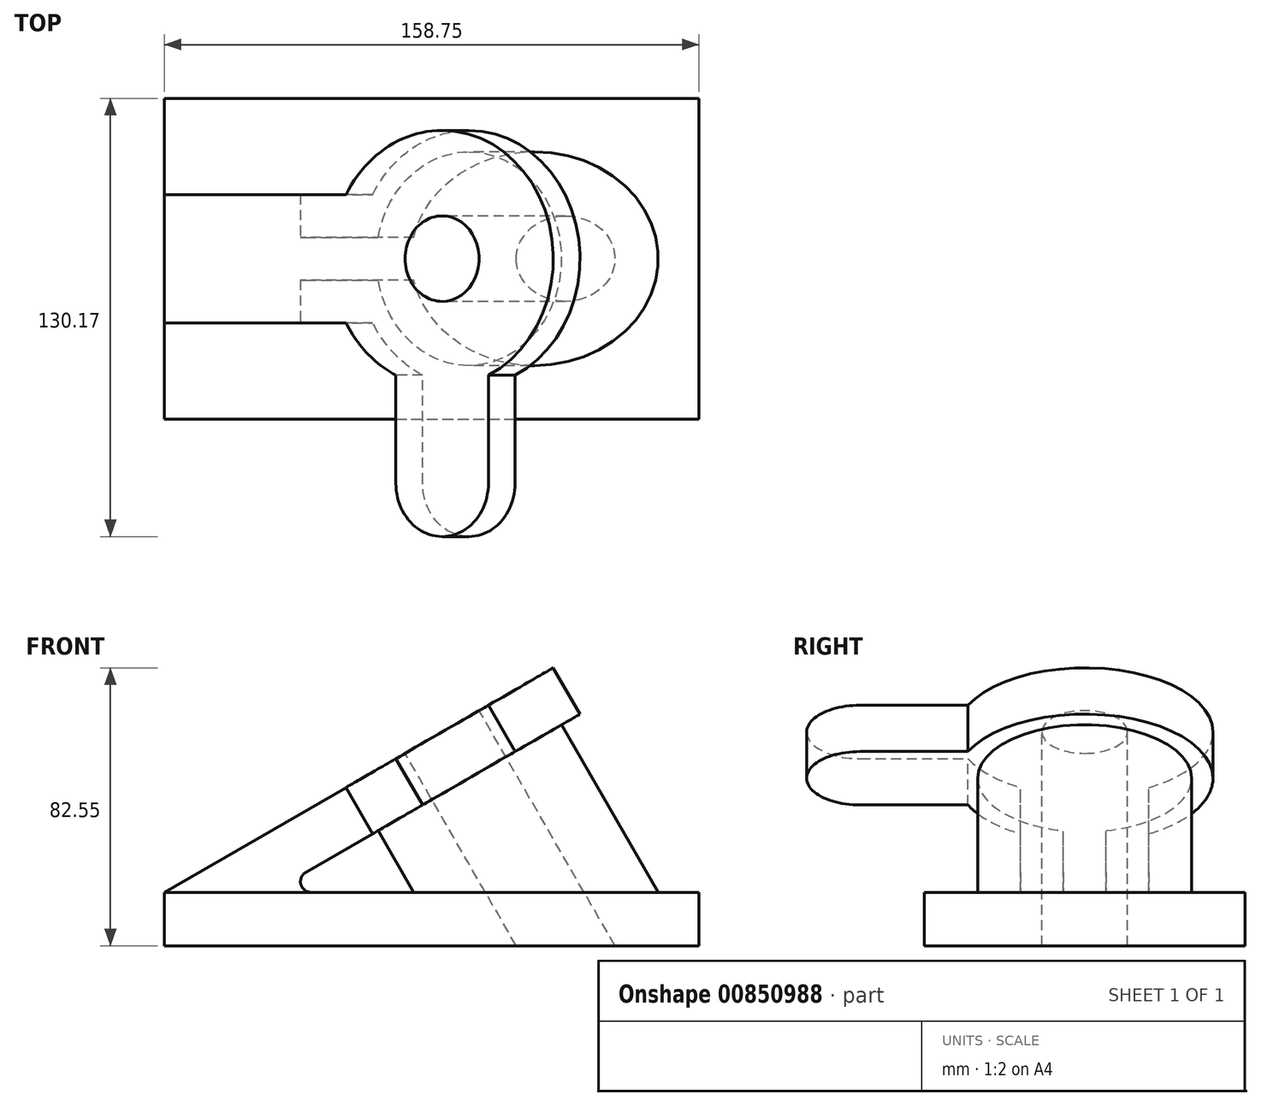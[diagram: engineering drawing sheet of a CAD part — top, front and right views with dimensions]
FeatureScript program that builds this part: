
annotation { "Feature Type Name" : "Feature", "Feature Type Description" : "" }
export const myFeature = defineFeature(function(context is Context, id is Id, definition is map)
    precondition{}
    {
        {
            var Q0;
            Q0=qCreatedBy(makeId("Front.planeOp"),FACE);
            var sketch = newSketch(context, id + "F0", { "sketchPlane" : qUnion([Q0])});
            skLineSegment(sketch, "E0.bottom", {"start": v(0, 0) * mm, "end": v(158.75, 0) * mm});
            skLineSegment(sketch, "E0.top", {"start": v(0, 15.88) * mm, "end": v(158.75, 15.88) * mm});
            skLineSegment(sketch, "E0.left", {"start": v(0, 0) * mm, "end": v(0, 15.87) * mm});
            skLineSegment(sketch, "E0.right", {"start": v(158.75, 0) * mm, "end": v(158.75, 15.88) * mm});
            skSolve(sketch);
        }
        {
            var Q0;
            Q0 = qSketchRegion(id + "F0", true);
            extrude(context, id + "F1", {"entities" : qUnion([Q0]), "oppositeDirection" : true, "depth" : 95.25 * mm, "offsetDistance" : 25.4 * mm});
        }
        {
            var Q0;
            Q0=makeQuery(id+"F1.opExtrude","SWEPT_EDGE",EDGE,{"disambiguationData":[OSD([sQuery(id+"F0.wireOp",EDGE,"E0.top"),sQuery(id+"F0.wireOp",EDGE,"E0.left")])]});
            var Q1;
            Q1=makeQuery(id+"F1.opExtrude","SWEPT_FACE",FACE,{"disambiguationData":[OSD([sQuery(id+"F0.wireOp",EDGE,"E0.top")])]});
            cPlane(context, id + "F2", {"entities" : qUnion([Q0, Q1]), "cplaneType" : CPlaneType.LINE_ANGLE, "offset" : 25.4 * mm, "angle" : 30 * degree, "width" : 152.4 * mm, "height" : 152.4 * mm});
        }
        {
            var Q0;
            Q0=qCreatedBy(id+"F2.planeOp",FACE);
            var sketch = newSketch(context, id + "F3", { "sketchPlane" : qUnion([Q0])});
            skArc(sketch, "E1", {"start": v(70.2, -66.67) * mm, "mid": v(131.36, -73.27) * mm, "end": v(119.06, -12.99) * mm});
            skLineSegment(sketch, "E2.bottom", {"start": v(7.94, -28.57) * mm, "end": v(70.2, -28.57) * mm});
            skLineSegment(sketch, "E2.top", {"start": v(7.94, -66.67) * mm, "end": v(70.2, -66.67) * mm});
            skLineSegment(sketch, "E2.left", {"start": v(7.94, -28.57) * mm, "end": v(7.94, -66.67) * mm});
            skPoint(sketch, "E2.middle", {"position": v(65.09, -47.63) * mm});
            skCircle(sketch, "E3", {"center": v(103.19, -47.63) * mm, "radius": 12.7 * mm});
            skArc(sketch, "E4", {"start": v(119.06, 19.05) * mm, "mid": v(103.19, 34.93) * mm, "end": v(87.31, 19.05) * mm});
            skLineSegment(sketch, "E5", {"start": v(119.06, 19.05) * mm, "end": v(119.06, -12.99) * mm});
            skLineSegment(sketch, "E6", {"start": v(87.31, 19.05) * mm, "end": v(87.31, -12.99) * mm});
            skArc(sketch, "E7.trimOffspring", {"start": v(87.31, -12.99) * mm, "mid": v(77.54, -19.45) * mm, "end": v(70.2, -28.58) * mm});
            skSolve(sketch);
        }
        {
            var Q0;
            Q0 = qSketchRegion(id + "F3", true);
            extrude(context, id + "F4", {"entities" : qUnion([Q0]), "operationType" : NewBodyOperationType.ADD, "depth" : 15.88 * mm, "offsetDistance" : 25.4 * mm});
        }
        {
            var Q0;
            Q0=makeQuery(id+"F4.opExtrude","CAP_FACE",FACE,{"disambiguationData":[OSD([sQuery(id+"F3.wireOp",EDGE,"E1"),sQuery(id+"F3.wireOp",EDGE,"E2.bottom"),sQuery(id+"F3.wireOp",EDGE,"E2.top"),sQuery(id+"F3.wireOp",EDGE,"E2.left"),sQuery(id+"F3.wireOp",EDGE,"E3"),sQuery(id+"F3.wireOp",EDGE,"E4"),sQuery(id+"F3.wireOp",EDGE,"E5"),sQuery(id+"F3.wireOp",EDGE,"E6"),sQuery(id+"F3.wireOp",EDGE,"E7.trimOffspring")])],"isStart":false});
            var sketch = newSketch(context, id + "F5", { "sketchPlane" : qUnion([Q0])});
            skCircle(sketch, "E8", {"center": v(103.19, -47.63) * mm, "radius": 12.7 * mm});
            skCircle(sketch, "E9", {"center": v(103.19, -47.63) * mm, "radius": 31.75 * mm});
            skSolve(sketch);
        }
        {
            var Q0;
            Q0=makeQuery(id+"F5.imprint","IMPRINT",FACE,{"disambiguationData":[TD([[makeQuery(id+"F5.imprint","IMPRINT",EDGE,{"derivedFrom":sQuery(id+"F5.wireOp",EDGE,"E8")}),-1.0]])]});
            var Q1;
            Q1=makeQuery(id+"F1.opExtrude","SWEPT_FACE",FACE,{"disambiguationData":[OSD([sQuery(id+"F0.wireOp",EDGE,"E0.top")])]});
            extrude(context, id + "F6", {"entities" : qUnion([Q0]), "operationType" : NewBodyOperationType.ADD, "endBound" : BoundingType.UP_TO_SURFACE, "depth" : 25.4 * mm, "endBoundEntityFace" : qUnion([Q1]), "offsetDistance" : 25.4 * mm});
        }
        {
            var Q0;
            Q0=makeQuery(id+"F4.opExtrude","CAP_FACE",FACE,{"disambiguationData":[OSD([sQuery(id+"F3.wireOp",EDGE,"E1"),sQuery(id+"F3.wireOp",EDGE,"E2.bottom"),sQuery(id+"F3.wireOp",EDGE,"E2.top"),sQuery(id+"F3.wireOp",EDGE,"E2.left"),sQuery(id+"F3.wireOp",EDGE,"E3"),sQuery(id+"F3.wireOp",EDGE,"E4"),sQuery(id+"F3.wireOp",EDGE,"E5"),sQuery(id+"F3.wireOp",EDGE,"E6"),sQuery(id+"F3.wireOp",EDGE,"E7.trimOffspring")])],"isStart":true});
            var sketch = newSketch(context, id + "F7", { "sketchPlane" : qUnion([Q0])});
            skCircle(sketch, "E10", {"center": v(103.19, 47.63) * mm, "radius": 12.7 * mm});
            skSolve(sketch);
        }
        {
            var Q0;
            Q0=makeQuery(id+"F7.imprint","IMPRINT",FACE,{"disambiguationData":[TD([[makeQuery(id+"F7.imprint","IMPRINT",EDGE,{"derivedFrom":sQuery(id+"F7.wireOp",EDGE,"E10")}),-1.0]])]});
            extrude(context, id + "F8", {"entities" : qUnion([Q0]), "operationType" : NewBodyOperationType.REMOVE, "endBound" : BoundingType.THROUGH_ALL, "oppositeDirection" : true, "depth" : 25.4 * mm, "offsetDistance" : 25.4 * mm});
        }
        {
            var Q0;
            {var subQ1=sQuery(id+"F0.wireOp",EDGE,"E0.left");var subQ2=sQuery(id+"F0.wireOp",EDGE,"E0.top");Q0=makeQuery(id+"F6.boolean.opBoolean","SPLIT",FACE,{"disambiguationData":[TD([makeQuery(id+"F1.opExtrude","SWEPT_FACE",FACE,{"disambiguationData":[OSD([subQ1])]})])],"derivedFrom":makeQuery(id+"F1.opExtrude","SWEPT_FACE",FACE,{"disambiguationData":[OSD([subQ2])]})});}
            var sketch = newSketch(context, id + "F9", { "sketchPlane" : qUnion([Q0])});
            skLineSegment(sketch, "E11.bottom", {"start": v(74.06, 41.28) * mm, "end": v(31.75, 41.28) * mm});
            skLineSegment(sketch, "E11.top", {"start": v(74.06, 53.98) * mm, "end": v(31.75, 53.98) * mm});
            skLineSegment(sketch, "E11.left", {"start": v(74.06, 41.28) * mm, "end": v(74.06, 53.98) * mm});
            skPoint(sketch, "E11.middle", {"position": v(31.75, 47.62) * mm});
            skLineSegment(sketch, "E12", {"start": v(31.75, 53.98) * mm, "end": v(31.75, 41.28) * mm});
            skSolve(sketch);
        }
        {
            var Q0;
            {var subQ0=sQuery(id+"F9.wireOp",EDGE,"E11.bottom");Q0=makeQuery(id+"F9.imprint","IMPRINT",FACE,{"disambiguationData":[TD([[makeQuery(id+"F9.imprint","IMPRINT",EDGE,{"derivedFrom":subQ0}),-1.0]])]});}
            var Q1;
            Q1=makeQuery(id+"F4.opExtrude","CAP_FACE",FACE,{"disambiguationData":[OSD([sQuery(id+"F3.wireOp",EDGE,"E1"),sQuery(id+"F3.wireOp",EDGE,"E2.bottom"),sQuery(id+"F3.wireOp",EDGE,"E2.top"),sQuery(id+"F3.wireOp",EDGE,"E2.left"),sQuery(id+"F3.wireOp",EDGE,"E3"),sQuery(id+"F3.wireOp",EDGE,"E4"),sQuery(id+"F3.wireOp",EDGE,"E5"),sQuery(id+"F3.wireOp",EDGE,"E6"),sQuery(id+"F3.wireOp",EDGE,"E7.trimOffspring")])],"isStart":false});
            extrude(context, id + "F10", {"entities" : qUnion([Q0]), "operationType" : NewBodyOperationType.ADD, "endBound" : BoundingType.UP_TO_SURFACE, "depth" : 25.4 * mm, "endBoundEntityFace" : qUnion([Q1]), "offsetDistance" : 25.4 * mm});
        }
        {
            var Q0;
            {var subQ0=makeQuery(id+"F1.opExtrude","SWEPT_FACE",FACE,{"disambiguationData":[OSD([sQuery(id+"F0.wireOp",EDGE,"E0.top")])]});var subQ1=sQuery(id+"F3.wireOp",EDGE,"E2.bottom");var subQ2=makeQuery(id+"F4.opExtrude","CAP_FACE",FACE,{"disambiguationData":[OSD([sQuery(id+"F3.wireOp",EDGE,"E1"),subQ1,sQuery(id+"F3.wireOp",EDGE,"E2.top"),sQuery(id+"F3.wireOp",EDGE,"E2.left"),sQuery(id+"F3.wireOp",EDGE,"E3"),sQuery(id+"F3.wireOp",EDGE,"E4"),sQuery(id+"F3.wireOp",EDGE,"E5"),sQuery(id+"F3.wireOp",EDGE,"E6"),sQuery(id+"F3.wireOp",EDGE,"E7.trimOffspring")])],"isStart":false});Q0=makeQuery(id+"F10.boolean.opBoolean","SPLIT",EDGE,{"disambiguationData":[TD([makeQuery(id+"F4.opExtrude","SWEPT_FACE",FACE,{"disambiguationData":[OSD([subQ1])]})])],"derivedFrom":makeQuery(id+"F4.boolean.opBoolean","INTERSECT",EDGE,{"derivedFrom":[subQ0,subQ2]})});}
            var Q1;
            {var subQ0=makeQuery(id+"F1.opExtrude","SWEPT_FACE",FACE,{"disambiguationData":[OSD([sQuery(id+"F0.wireOp",EDGE,"E0.top")])]});var subQ1=sQuery(id+"F3.wireOp",EDGE,"E2.top");var subQ2=makeQuery(id+"F4.opExtrude","CAP_FACE",FACE,{"disambiguationData":[OSD([sQuery(id+"F3.wireOp",EDGE,"E1"),sQuery(id+"F3.wireOp",EDGE,"E2.bottom"),subQ1,sQuery(id+"F3.wireOp",EDGE,"E2.left"),sQuery(id+"F3.wireOp",EDGE,"E3"),sQuery(id+"F3.wireOp",EDGE,"E4"),sQuery(id+"F3.wireOp",EDGE,"E5"),sQuery(id+"F3.wireOp",EDGE,"E6"),sQuery(id+"F3.wireOp",EDGE,"E7.trimOffspring")])],"isStart":false});Q1=makeQuery(id+"F10.boolean.opBoolean","SPLIT",EDGE,{"disambiguationData":[TD([makeQuery(id+"F4.opExtrude","SWEPT_FACE",FACE,{"disambiguationData":[OSD([subQ1])]})])],"derivedFrom":makeQuery(id+"F4.boolean.opBoolean","INTERSECT",EDGE,{"derivedFrom":[subQ0,subQ2]})});}
            fillet(context, id + "F11", {"entities" : qUnion([Q0, Q1]), "radius" : 3.17 * mm, "tangentPropagation" : true, "allowEdgeOverflow" : false});
        }
    });
